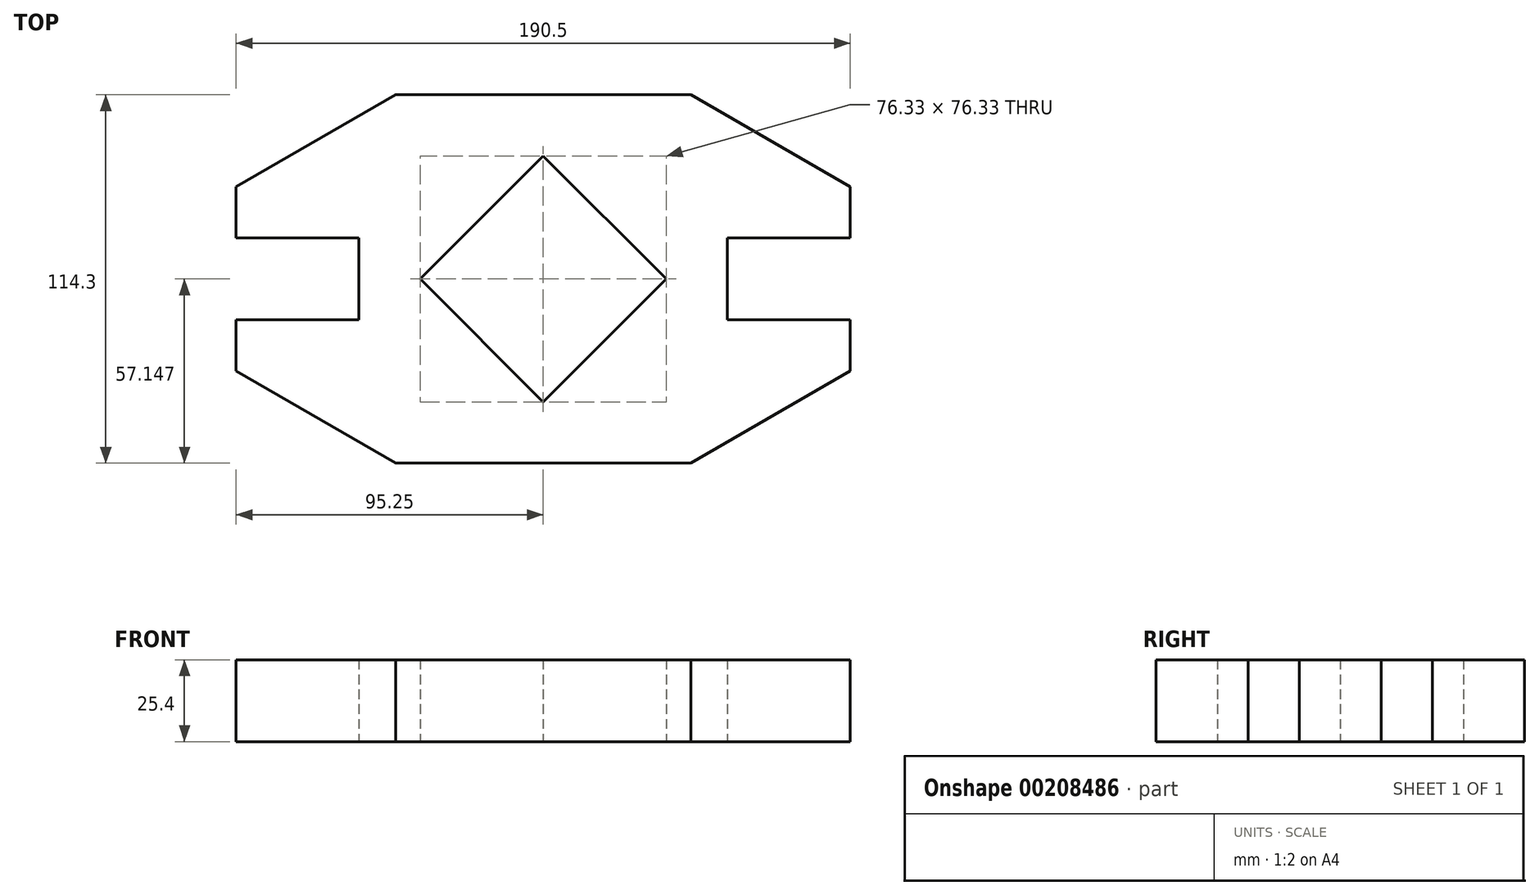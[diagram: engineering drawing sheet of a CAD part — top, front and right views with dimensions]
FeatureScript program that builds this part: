
annotation { "Feature Type Name" : "Feature", "Feature Type Description" : "" }
export const myFeature = defineFeature(function(context is Context, id is Id, definition is map)
    precondition{}
    {
        {
            var Q0;
            Q0=qCreatedBy(makeId("Top.planeOp"),FACE);
            var sketch = newSketch(context, id + "F0", { "sketchPlane" : qUnion([Q0])});
            skLineSegment(sketch, "E0", {"start": v(-152.4, 86.53) * mm, "end": v(38.1, 86.53) * mm, "construction": true});
            skLineSegment(sketch, "E1", {"start": v(38.1, 86.53) * mm, "end": v(38.1, -27.77) * mm, "construction": true});
            skLineSegment(sketch, "E2", {"start": v(-152.4, 86.53) * mm, "end": v(-152.4, -27.77) * mm, "construction": true});
            skLineSegment(sketch, "E3", {"start": v(-152.4, -27.77) * mm, "end": v(38.1, -27.77) * mm, "construction": true});
            skLineSegment(sketch, "E4", {"start": v(-152.4, 29.38) * mm, "end": v(38.1, 29.38) * mm, "construction": true});
            skLineSegment(sketch, "E5", {"start": v(-57.15, 86.53) * mm, "end": v(-57.15, -27.77) * mm, "construction": true});
            skLineSegment(sketch, "E6", {"start": v(-95.32, 29.38) * mm, "end": v(-57.15, 67.54) * mm});
            skLineSegment(sketch, "E7", {"start": v(-95.32, 29.38) * mm, "end": v(-57.15, -8.79) * mm});
            skLineSegment(sketch, "E8", {"start": v(-57.15, 67.54) * mm, "end": v(-18.98, 29.38) * mm});
            skLineSegment(sketch, "E9", {"start": v(-57.15, -8.79) * mm, "end": v(-18.98, 29.38) * mm});
            skLineSegment(sketch, "E10", {"start": v(-152.4, 86.53) * mm, "end": v(-116.27, 86.53) * mm});
            skLineSegment(sketch, "E11", {"start": v(0, 29.38) * mm, "end": v(0, 42.08) * mm});
            skLineSegment(sketch, "E12", {"start": v(0, 42.08) * mm, "end": v(38.1, 42.08) * mm});
            skLineSegment(sketch, "E13.MirrorCS", {"start": v(0, 29.38) * mm, "end": v(0, 16.68) * mm});
            skLineSegment(sketch, "E14.MirrorCS", {"start": v(0, 16.68) * mm, "end": v(38.1, 16.68) * mm});
            skLineSegment(sketch, "E15.MirrorCS", {"start": v(-114.3, 42.08) * mm, "end": v(-152.4, 42.08) * mm});
            skLineSegment(sketch, "E16.MirrorCS", {"start": v(-114.3, 29.38) * mm, "end": v(-114.3, 42.08) * mm});
            skLineSegment(sketch, "E17.MirrorCS", {"start": v(-114.3, 29.38) * mm, "end": v(-114.3, 16.68) * mm});
            skLineSegment(sketch, "E18.MirrorCS", {"start": v(-114.3, 16.68) * mm, "end": v(-152.4, 16.68) * mm});
            skLineSegment(sketch, "E19", {"start": v(38.1, 42.08) * mm, "end": v(38.1, 57.95) * mm});
            skLineSegment(sketch, "E20", {"start": v(38.1, 57.95) * mm, "end": v(-11.4, 86.53) * mm});
            skLineSegment(sketch, "E21.MirrorCS", {"start": v(38.1, 16.68) * mm, "end": v(38.1, 0.8) * mm});
            skLineSegment(sketch, "E22.MirrorCS", {"start": v(38.1, 0.8) * mm, "end": v(-11.4, -27.77) * mm});
            skLineSegment(sketch, "E23.MirrorCS", {"start": v(-152.4, 57.95) * mm, "end": v(-102.9, 86.53) * mm});
            skLineSegment(sketch, "E24.MirrorCS", {"start": v(-152.4, 42.08) * mm, "end": v(-152.4, 57.95) * mm});
            skLineSegment(sketch, "E25.MirrorCS", {"start": v(-152.4, 16.68) * mm, "end": v(-152.4, 0.8) * mm});
            skLineSegment(sketch, "E26.MirrorCS", {"start": v(-152.4, 0.8) * mm, "end": v(-102.9, -27.77) * mm});
            skLineSegment(sketch, "E27", {"start": v(-102.9, 86.53) * mm, "end": v(-11.4, 86.53) * mm});
            skLineSegment(sketch, "E28", {"start": v(-102.9, -27.77) * mm, "end": v(-11.4, -27.77) * mm});
            skSolve(sketch);
        }
        {
            var Q0;
            Q0=makeQuery(id+"F0.imprint","IMPRINT",FACE,{"disambiguationData":[TD([[makeQuery(id+"F0.imprint","IMPRINT",EDGE,{"derivedFrom":sQuery(id+"F0.wireOp",EDGE,"E6")}),1.0]])]});
            extrude(context, id + "F1", {"entities" : qUnion([Q0]), "depth" : 25.4 * mm});
        }
    });
